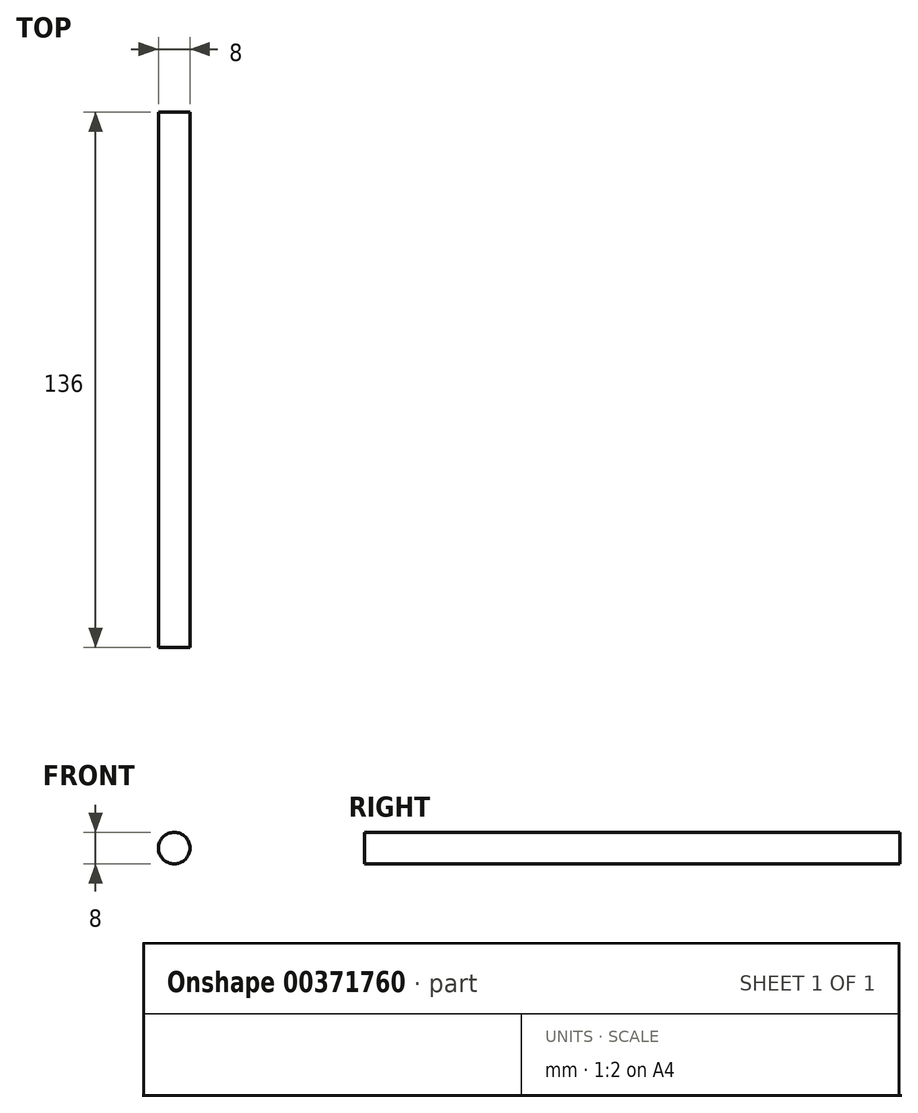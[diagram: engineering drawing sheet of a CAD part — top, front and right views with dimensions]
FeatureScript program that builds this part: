
annotation { "Feature Type Name" : "Feature", "Feature Type Description" : "" }
export const myFeature = defineFeature(function(context is Context, id is Id, definition is map)
    precondition{}
    {
        {
            var Q0;
            Q0=qCreatedBy(makeId("Front.planeOp"),FACE);
            var sketch = newSketch(context, id + "F0", { "sketchPlane" : qUnion([Q0])});
            skCircle(sketch, "E0", {"center": v(0, 0) * mm, "radius": 4 * mm});
            skSolve(sketch);
        }
        {
            assignVariable(context, id + "F1", {"name" : "x", "anyValue" : 136});
        }
        {
            var Q0;
            Q0=makeQuery(id+"F0.imprint","IMPRINT",FACE,{"disambiguationData":[TD([[makeQuery(id+"F0.imprint","IMPRINT",EDGE,{"derivedFrom":sQuery(id+"F0.wireOp",EDGE,"E0")}),1.0]])]});
            extrude(context, id + "F2", {"entities" : qUnion([Q0]), "depth" : (getVariable(context, 'x')) * mm});
        }
    });
